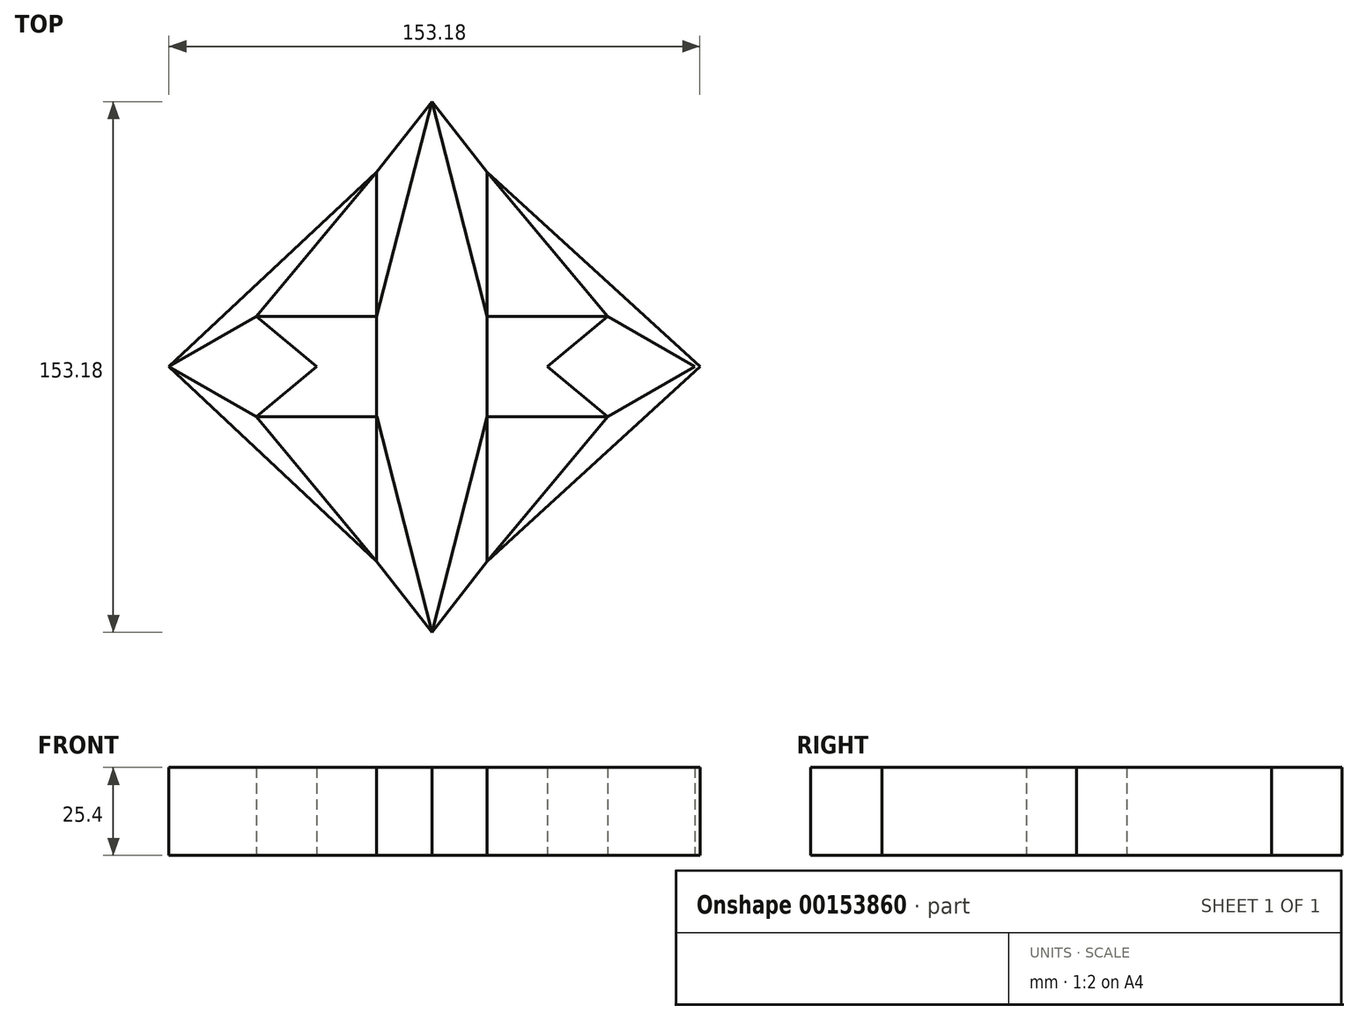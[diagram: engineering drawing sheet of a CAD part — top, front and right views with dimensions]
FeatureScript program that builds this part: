
annotation { "Feature Type Name" : "Feature", "Feature Type Description" : "" }
export const myFeature = defineFeature(function(context is Context, id is Id, definition is map)
    precondition{}
    {
        {
            var Q0;
            Q0=qCreatedBy(makeId("Top.planeOp"),FACE);
            var sketch = newSketch(context, id + "F0", { "sketchPlane" : qUnion([Q0])});
            skLineSegment(sketch, "E0.bottom", {"start": v(50.65, -14.46) * mm, "end": v(-50.65, -14.46) * mm});
            skLineSegment(sketch, "E0.top", {"start": v(50.65, 14.46) * mm, "end": v(-50.65, 14.46) * mm});
            skLineSegment(sketch, "E0.left", {"start": v(50.65, -14.46) * mm, "end": v(50.65, 14.46) * mm});
            skLineSegment(sketch, "E0.right", {"start": v(-50.65, -14.46) * mm, "end": v(-50.65, 14.46) * mm});
            skPoint(sketch, "E0.middle", {"position": v(0, 0) * mm});
            skLineSegment(sketch, "E1.bottom", {"start": v(15.95, 56.17) * mm, "end": v(-15.95, 56.17) * mm});
            skLineSegment(sketch, "E1.top", {"start": v(15.95, -56.17) * mm, "end": v(-15.95, -56.17) * mm});
            skLineSegment(sketch, "E1.left", {"start": v(15.95, 56.17) * mm, "end": v(15.95, -56.17) * mm});
            skLineSegment(sketch, "E1.right", {"start": v(-15.95, 56.17) * mm, "end": v(-15.95, -56.17) * mm});
            skLineSegment(sketch, "E2", {"start": v(-50.65, 14.46) * mm, "end": v(-15.95, 56.17) * mm});
            skLineSegment(sketch, "E3", {"start": v(15.95, 56.17) * mm, "end": v(50.65, 14.46) * mm});
            skLineSegment(sketch, "E4", {"start": v(50.65, -14.46) * mm, "end": v(15.95, -56.17) * mm});
            skLineSegment(sketch, "E5", {"start": v(-15.95, -56.17) * mm, "end": v(-50.65, -14.46) * mm});
            skLineSegment(sketch, "E6", {"start": v(50.65, 14.46) * mm, "end": v(75.9, 0) * mm});
            skLineSegment(sketch, "E7", {"start": v(75.9, 0) * mm, "end": v(50.65, -14.46) * mm});
            skArc(sketch, "E8", {"start": v(50.65, 14.46) * mm, "mid": v(40.84, 41.6) * mm, "end": v(15.95, 56.17) * mm});
            skArc(sketch, "E9", {"start": v(-50.65, 14.46) * mm, "mid": v(-40.84, 41.6) * mm, "end": v(-15.95, 56.17) * mm});
            skArc(sketch, "E10", {"start": v(15.95, -56.17) * mm, "mid": v(43.08, -43.45) * mm, "end": v(50.65, -14.46) * mm});
            skArc(sketch, "E11", {"start": v(-15.95, -56.17) * mm, "mid": v(-43.08, -43.45) * mm, "end": v(-50.65, -14.46) * mm});
            skLineSegment(sketch, "E12", {"start": v(-50.65, 14.46) * mm, "end": v(-15.9, -14.46) * mm});
            skLineSegment(sketch, "E13", {"start": v(50.65, 14.46) * mm, "end": v(15.95, -14.46) * mm});
            skLineSegment(sketch, "E14", {"start": v(15.95, -56.17) * mm, "end": v(77.3, 0) * mm});
            skLineSegment(sketch, "E15", {"start": v(77.3, 0) * mm, "end": v(15.95, 56.17) * mm});
            skLineSegment(sketch, "E16", {"start": v(-15.95, -56.17) * mm, "end": v(0, -76.68) * mm});
            skLineSegment(sketch, "E17", {"start": v(0, -76.68) * mm, "end": v(15.95, -56.17) * mm});
            skLineSegment(sketch, "E18", {"start": v(0, -76.68) * mm, "end": v(-15.9, -14.46) * mm});
            skLineSegment(sketch, "E19", {"start": v(0, -76.68) * mm, "end": v(15.95, -14.46) * mm});
            skLineSegment(sketch, "E20", {"start": v(-50.65, 14.46) * mm, "end": v(-75.9, 0) * mm});
            skLineSegment(sketch, "E21", {"start": v(-75.9, 0) * mm, "end": v(-50.65, -14.46) * mm});
            skLineSegment(sketch, "E22", {"start": v(-75.9, 0) * mm, "end": v(-15.95, -56.17) * mm});
            skLineSegment(sketch, "E23", {"start": v(-75.9, 0) * mm, "end": v(-15.95, 56.17) * mm});
            skLineSegment(sketch, "E24", {"start": v(-15.95, 56.17) * mm, "end": v(0, 76.5) * mm});
            skLineSegment(sketch, "E25", {"start": v(0, 76.5) * mm, "end": v(15.95, 56.17) * mm});
            skLineSegment(sketch, "E26", {"start": v(0, 76.5) * mm, "end": v(-15.95, 14.46) * mm});
            skLineSegment(sketch, "E27", {"start": v(0, 76.5) * mm, "end": v(15.95, 14.46) * mm});
            skLineSegment(sketch, "E28", {"start": v(-15.95, 14.46) * mm, "end": v(-50.65, -14.46) * mm});
            skLineSegment(sketch, "E29", {"start": v(15.95, 14.46) * mm, "end": v(50.65, -14.46) * mm});
            skSolve(sketch);
        }
        {
            var Q0;
            {var subQ0=sQuery(id+"F0.wireOp",EDGE,"E25");Q0=makeQuery(id+"F0.imprint","IMPRINT",FACE,{"disambiguationData":[TD([[makeQuery(id+"F0.imprint","IMPRINT",EDGE,{"derivedFrom":subQ0}),-1.0]])]});}
            var Q1;
            {var subQ0=sQuery(id+"F0.wireOp",EDGE,"E24");Q1=makeQuery(id+"F0.imprint","IMPRINT",FACE,{"disambiguationData":[TD([[makeQuery(id+"F0.imprint","IMPRINT",EDGE,{"derivedFrom":subQ0}),-1.0]])]});}
            var Q2;
            {var subQ0=sQuery(id+"F0.wireOp",EDGE,"E17");Q2=makeQuery(id+"F0.imprint","IMPRINT",FACE,{"disambiguationData":[TD([[makeQuery(id+"F0.imprint","IMPRINT",EDGE,{"derivedFrom":subQ0}),1.0]])]});}
            var Q3;
            {var subQ0=sQuery(id+"F0.wireOp",EDGE,"E16");Q3=makeQuery(id+"F0.imprint","IMPRINT",FACE,{"disambiguationData":[TD([[makeQuery(id+"F0.imprint","IMPRINT",EDGE,{"derivedFrom":subQ0}),1.0]])]});}
            var Q4;
            {var subQ0=sQuery(id+"F0.wireOp",EDGE,"E20");Q4=makeQuery(id+"F0.imprint","IMPRINT",FACE,{"disambiguationData":[TD([[makeQuery(id+"F0.imprint","IMPRINT",EDGE,{"derivedFrom":subQ0}),-1.0]])]});}
            var Q5;
            {var subQ0=sQuery(id+"F0.wireOp",EDGE,"E21");Q5=makeQuery(id+"F0.imprint","IMPRINT",FACE,{"disambiguationData":[TD([[makeQuery(id+"F0.imprint","IMPRINT",EDGE,{"derivedFrom":subQ0}),-1.0]])]});}
            var Q6;
            {var subQ1=sQuery(id+"F0.wireOp",EDGE,"E1.bottom");var subQ3=sQuery(id+"F0.wireOp",EDGE,"E27");var subQ4=makeQuery(id+"F0.imprint","INTERSECT",VERTEX,{"derivedFrom":[subQ1,subQ3]});Q6=makeQuery(id+"F0.imprint","IMPRINT",FACE,{"disambiguationData":[TD([[makeQuery(id+"F0.imprint","IMPRINT",EDGE,{"disambiguationData":[TD([[subQ4,-1.0]])],"derivedFrom":subQ3}),1.0]])]});}
            var Q7;
            {var subQ1=sQuery(id+"F0.wireOp",EDGE,"E1.bottom");var subQ3=sQuery(id+"F0.wireOp",EDGE,"E26");var subQ4=makeQuery(id+"F0.imprint","INTERSECT",VERTEX,{"derivedFrom":[subQ1,subQ3]});Q7=makeQuery(id+"F0.imprint","IMPRINT",FACE,{"disambiguationData":[TD([[makeQuery(id+"F0.imprint","IMPRINT",EDGE,{"disambiguationData":[TD([[subQ4,-1.0]])],"derivedFrom":subQ3}),-1.0]])]});}
            var Q8;
            {var subQ1=sQuery(id+"F0.wireOp",EDGE,"E1.top");var subQ3=sQuery(id+"F0.wireOp",EDGE,"E19");var subQ4=makeQuery(id+"F0.imprint","INTERSECT",VERTEX,{"derivedFrom":[subQ1,subQ3]});Q8=makeQuery(id+"F0.imprint","IMPRINT",FACE,{"disambiguationData":[TD([[makeQuery(id+"F0.imprint","IMPRINT",EDGE,{"disambiguationData":[TD([[subQ4,-1.0]])],"derivedFrom":subQ3}),-1.0]])]});}
            var Q9;
            {var subQ0=sQuery(id+"F0.wireOp",EDGE,"E2");Q9=makeQuery(id+"F0.imprint","IMPRINT",FACE,{"disambiguationData":[TD([[makeQuery(id+"F0.imprint","IMPRINT",EDGE,{"derivedFrom":subQ0}),1.0]])]});}
            var Q10;
            {var subQ0=sQuery(id+"F0.wireOp",EDGE,"E3");Q10=makeQuery(id+"F0.imprint","IMPRINT",FACE,{"disambiguationData":[TD([[makeQuery(id+"F0.imprint","IMPRINT",EDGE,{"derivedFrom":subQ0}),1.0]])]});}
            var Q11;
            {var subQ0=sQuery(id+"F0.wireOp",EDGE,"E4");Q11=makeQuery(id+"F0.imprint","IMPRINT",FACE,{"disambiguationData":[TD([[makeQuery(id+"F0.imprint","IMPRINT",EDGE,{"derivedFrom":subQ0}),1.0]])]});}
            var Q12;
            {var subQ0=sQuery(id+"F0.wireOp",EDGE,"E5");Q12=makeQuery(id+"F0.imprint","IMPRINT",FACE,{"disambiguationData":[TD([[makeQuery(id+"F0.imprint","IMPRINT",EDGE,{"derivedFrom":subQ0}),1.0]])]});}
            var Q13;
            {var subQ6=sQuery(id+"F0.wireOp",EDGE,"E6");Q13=makeQuery(id+"F0.imprint","IMPRINT",FACE,{"disambiguationData":[TD([[makeQuery(id+"F0.imprint","IMPRINT",EDGE,{"derivedFrom":subQ6}),1.0]])]});}
            var Q14;
            {var subQ1=sQuery(id+"F0.wireOp",EDGE,"E0.bottom");var subQ3=sQuery(id+"F0.wireOp",EDGE,"E1.right");var subQ4=makeQuery(id+"F0.imprint","INTERSECT",VERTEX,{"derivedFrom":[subQ1,subQ3]});Q14=makeQuery(id+"F0.imprint","IMPRINT",FACE,{"disambiguationData":[TD([[makeQuery(id+"F0.imprint","IMPRINT",EDGE,{"disambiguationData":[TD([[subQ4,1.0]])],"derivedFrom":subQ1}),1.0]])]});}
            var Q15;
            {var subQ0=sQuery(id+"F0.wireOp",EDGE,"E13");var subQ3=sQuery(id+"F0.wireOp",EDGE,"E29");var subQ5=makeQuery(id+"F0.imprint","INTERSECT",VERTEX,{"derivedFrom":[subQ0,subQ3]});Q15=makeQuery(id+"F0.imprint","IMPRINT",FACE,{"disambiguationData":[TD([[makeQuery(id+"F0.imprint","IMPRINT",EDGE,{"disambiguationData":[TD([[subQ5,1.0]])],"derivedFrom":subQ3}),1.0]])]});}
            var Q16;
            {var subQ0=sQuery(id+"F0.wireOp",EDGE,"E29");var subQ3=sQuery(id+"F0.wireOp",EDGE,"E13");var subQ5=makeQuery(id+"F0.imprint","INTERSECT",VERTEX,{"derivedFrom":[subQ3,subQ0]});Q16=makeQuery(id+"F0.imprint","IMPRINT",FACE,{"disambiguationData":[TD([[makeQuery(id+"F0.imprint","IMPRINT",EDGE,{"disambiguationData":[TD([[subQ5,-1.0]])],"derivedFrom":subQ3}),1.0]])]});}
            var Q17;
            {var subQ0=sQuery(id+"F0.wireOp",EDGE,"E12");var subQ3=sQuery(id+"F0.wireOp",EDGE,"E28");var subQ5=makeQuery(id+"F0.imprint","INTERSECT",VERTEX,{"derivedFrom":[subQ0,subQ3]});Q17=makeQuery(id+"F0.imprint","IMPRINT",FACE,{"disambiguationData":[TD([[makeQuery(id+"F0.imprint","IMPRINT",EDGE,{"disambiguationData":[TD([[subQ5,1.0]])],"derivedFrom":subQ3}),-1.0]])]});}
            var Q18;
            {var subQ1=sQuery(id+"F0.wireOp",EDGE,"E0.bottom");var subQ3=sQuery(id+"F0.wireOp",EDGE,"E1.right");var subQ4=makeQuery(id+"F0.imprint","INTERSECT",VERTEX,{"derivedFrom":[subQ1,subQ3]});Q18=makeQuery(id+"F0.imprint","IMPRINT",FACE,{"disambiguationData":[TD([[makeQuery(id+"F0.imprint","IMPRINT",EDGE,{"disambiguationData":[TD([[subQ4,1.0]])],"derivedFrom":subQ3}),-1.0]])]});}
            var Q19;
            {var subQ0=sQuery(id+"F0.wireOp",EDGE,"E13");var subQ3=sQuery(id+"F0.wireOp",EDGE,"E29");var subQ5=makeQuery(id+"F0.imprint","INTERSECT",VERTEX,{"derivedFrom":[subQ0,subQ3]});Q19=makeQuery(id+"F0.imprint","IMPRINT",FACE,{"disambiguationData":[TD([[makeQuery(id+"F0.imprint","IMPRINT",EDGE,{"disambiguationData":[TD([[subQ5,-1.0]])],"derivedFrom":subQ0}),-1.0]])]});}
            var Q20;
            {var subQ1=sQuery(id+"F0.wireOp",EDGE,"E1.right");var subQ3=sQuery(id+"F0.wireOp",EDGE,"E12");var subQ4=makeQuery(id+"F0.imprint","INTERSECT",VERTEX,{"derivedFrom":[subQ1,subQ3]});Q20=makeQuery(id+"F0.imprint","IMPRINT",FACE,{"disambiguationData":[TD([[makeQuery(id+"F0.imprint","IMPRINT",EDGE,{"disambiguationData":[TD([[subQ4,1.0]])],"derivedFrom":subQ3}),1.0]])]});}
            extrude(context, id + "F1", {"entities" : qUnion([Q0, Q1, Q2, Q3, Q4, Q5, Q6, Q7, Q8, Q9, Q10, Q11, Q12, Q13, Q14, Q15, Q16, Q17, Q18, Q19, Q20]), "depth" : 25.4 * mm});
        }
    });
